# Revit family: DC_Rheem_PLM_HeavyDutyGas_620260
name_source: partatom
category: Plumbing Fixtures
revit_build: Autodesk Revit 2018 (Build: 20170223_1515(x64)
units: mm (PartAtom-declared; Revit-internal decimal feet)

## family parameters
Cut with Voids When Loaded = No
Host = Face
Part Type = Normal
Room Calculation Point = No
Round Connector Dimension = Use Radius
Shared = No

## types (2) — shared parameters
A1_ANZRS = 327 mm
ColdWaterPipeDiameterD4_ANZRS = 32 mm
ColdWaterPipeRadius_ANZRS = 16 mm  [stored 0.0524934 ft]
CylinderDiameterD3_ANZRS = 593 mm
CylinderRadius_ANZRS = 297 mm  [stored 0.974409 ft]
FireProofBase_ANZRS = 50 mm  [stored 0.164042 ft]
GasInletHeightH3_ANZRS = 297 mm  [stored 0.974409 ft]
GasPipeDiameterD2_ANZRS = 15 mm
GasPipeRadius_ANZRS = 8 mm  [stored 0.0262467 ft]
HeightH2_ANZRS = 1520 mm  [stored 4.98688 ft]
HotWaterPipeDiameterD1_ANZRS = 32 mm
HotWaterPipeHeightH2_ANZRS = 988 mm
HotWaterPipeRadius_ANZRS = 16 mm  [stored 0.0524934 ft]
Manufacturer = Rheem
Materials_ANZRS = Rheem - Joey Grey Steel
T&PRConnectionRadius_ANZRS = 20 mm  [stored 0.0656168 ft]
Thickness_ANZRS = 77 mm
TotalHeightH1_ANZRS = 1660 mm  [stored 5.44619 ft]
Type Comments = 385L first hour delivery @ 50oC rise
URL = http://www.rheem.com.au
zero-valued in all types: Default Elevation

## per-type parameters (varying)
| type | ColdWaterInletHeightH4_ANZRS | Description | Model |
| Heavy Duty Gas Storage - Indoor - 260L - 51 MJ/h - Natural gas | 278 mm | Heavy Duty Gas Storage - Indoor - 260L - 51 MJ/h - Natural gas | 620260N0 |
| Heavy Duty Gas Storage - Indoor - 260L - 47 MJ/h - Propane gas | 328 mm  [stored 1.07612 ft] | Heavy Duty Gas Storage - Indoor - 260L - 47 MJ/h - Propane gas
 Heavy Duty Gas Storage - Indoor - 260L - 47 MJ/h - Propane gas | 620260P0 |

note: [stored X ft] marks values corroborated as IEEE doubles in the binary element streams (Revit-internal decimal feet)

## geometry (parser evidence)
native form markers: Blend x4, Sweep x4
no freeform markers — native parametric forms only
